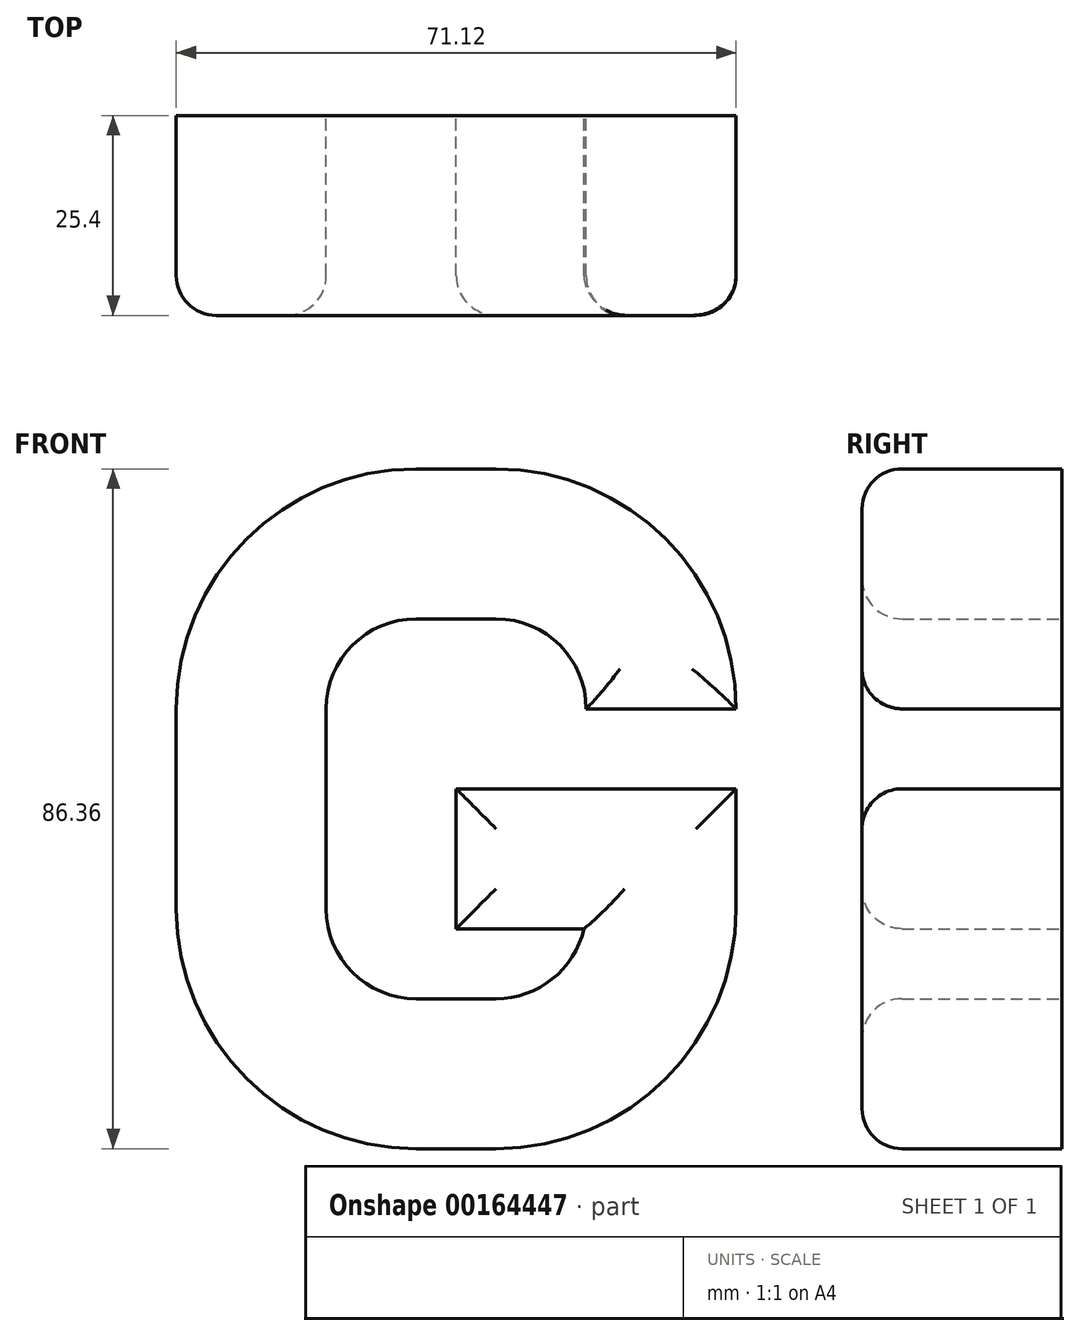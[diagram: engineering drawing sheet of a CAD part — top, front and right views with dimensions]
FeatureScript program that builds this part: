
annotation { "Feature Type Name" : "Feature", "Feature Type Description" : "" }
export const myFeature = defineFeature(function(context is Context, id is Id, definition is map)
    precondition{}
    {
        {
            var Q0;
            Q0=qCreatedBy(makeId("Front.planeOp"),FACE);
            var sketch = newSketch(context, id + "F0", { "sketchPlane" : qUnion([Q0])});
            skLineSegment(sketch, "E0.bottom", {"start": v(-5.08, 43.18) * mm, "end": v(5.08, 43.18) * mm});
            skLineSegment(sketch, "E0.top", {"start": v(-5.08, -43.18) * mm, "end": v(5.08, -43.18) * mm});
            skLineSegment(sketch, "E0.left", {"start": v(-35.56, 12.7) * mm, "end": v(-35.56, -12.7) * mm});
            skLineSegment(sketch, "E0.right", {"start": v(35.56, 0) * mm, "end": v(35.56, -12.7) * mm});
            skPoint(sketch, "E1.visualSharp", {"position": v(-35.56, 43.18) * mm});
            skArc(sketch, "E1.filletArc", {"start": v(-5.08, 43.18) * mm, "mid": v(-26.63, 34.25) * mm, "end": v(-35.56, 12.7) * mm});
            skPoint(sketch, "E2.visualSharp", {"position": v(-35.56, -43.18) * mm});
            skArc(sketch, "E2.filletArc", {"start": v(-35.56, -12.7) * mm, "mid": v(-26.63, -34.25) * mm, "end": v(-5.08, -43.18) * mm});
            skPoint(sketch, "E3.visualSharp", {"position": v(35.56, 43.18) * mm});
            skArc(sketch, "E3.filletArc", {"start": v(35.56, 12.7) * mm, "mid": v(26.63, 34.25) * mm, "end": v(5.08, 43.18) * mm});
            skPoint(sketch, "E4.visualSharp", {"position": v(35.56, -43.18) * mm});
            skArc(sketch, "E4.filletArc", {"start": v(5.08, -43.18) * mm, "mid": v(26.63, -34.25) * mm, "end": v(35.56, -12.7) * mm});
            skLineSegment(sketch, "E5.0", {"start": v(-5.08, -24.13) * mm, "end": v(5.08, -24.13) * mm});
            skArc(sketch, "E5.1", {"start": v(-16.51, -12.7) * mm, "mid": v(-13.16, -20.78) * mm, "end": v(-5.08, -24.13) * mm});
            skArc(sketch, "E5.2", {"start": v(5.08, -24.13) * mm, "mid": v(12.2, -21.64) * mm, "end": v(16.22, -15.24) * mm});
            skLineSegment(sketch, "E5.3", {"start": v(-16.51, 12.7) * mm, "end": v(-16.51, -12.7) * mm});
            skArc(sketch, "E5.5", {"start": v(16.51, 12.7) * mm, "mid": v(13.16, 20.78) * mm, "end": v(5.08, 24.13) * mm});
            skLineSegment(sketch, "E5.6", {"start": v(-5.08, 24.13) * mm, "end": v(5.08, 24.13) * mm});
            skArc(sketch, "E5.7", {"start": v(-5.08, 24.13) * mm, "mid": v(-13.16, 20.78) * mm, "end": v(-16.51, 12.7) * mm});
            skLineSegment(sketch, "E6", {"start": v(16.51, 12.7) * mm, "end": v(35.56, 12.7) * mm});
            skLineSegment(sketch, "E7", {"start": v(0, 0) * mm, "end": v(0, -12.7) * mm});
            skLineSegment(sketch, "E8", {"start": v(0, -12.7) * mm, "end": v(0, -15.24) * mm});
            skLineSegment(sketch, "E9", {"start": v(0, -15.24) * mm, "end": v(16.22, -15.24) * mm});
            skLineSegment(sketch, "E10", {"start": v(0, 0) * mm, "end": v(0, 2.54) * mm});
            skLineSegment(sketch, "E11", {"start": v(0, 2.54) * mm, "end": v(35.56, 2.54) * mm});
            skLineSegment(sketch, "E12", {"start": v(35.56, 0) * mm, "end": v(35.56, 2.54) * mm});
            skSolve(sketch);
        }
        {
            var Q0;
            Q0=makeQuery(id+"F0.imprint","IMPRINT",FACE,{"disambiguationData":[TD([[makeQuery(id+"F0.imprint","IMPRINT",EDGE,{"derivedFrom":sQuery(id+"F0.wireOp",EDGE,"E0.bottom")}),-1.0]])]});
            extrude(context, id + "F1", {"entities" : qUnion([Q0]), "depth" : 25.4 * mm});
        }
        {
            var Q0;
            Q0=makeQuery(id+"F1.opExtrude","CAP_EDGE",EDGE,{"disambiguationData":[OSD([sQuery(id+"F0.wireOp",EDGE,"E3.filletArc")])],"isStart":false});
            var Q1;
            Q1=makeQuery(id+"F1.opExtrude","CAP_EDGE",EDGE,{"disambiguationData":[OSD([sQuery(id+"F0.wireOp",EDGE,"E5.1")])],"isStart":false});
            var Q2;
            Q2=makeQuery(id+"F1.opExtrude","CAP_EDGE",EDGE,{"disambiguationData":[OSD([sQuery(id+"F0.wireOp",EDGE,"E9")])],"isStart":false});
            var Q3;
            Q3=makeQuery(id+"F1.opExtrude","CAP_EDGE",EDGE,{"disambiguationData":[OSD([sQuery(id+"F0.wireOp",EDGE,"E7"),sQuery(id+"F0.wireOp",EDGE,"E8"),sQuery(id+"F0.wireOp",EDGE,"E10")])],"isStart":false});
            var Q4;
            Q4=makeQuery(id+"F1.opExtrude","CAP_EDGE",EDGE,{"disambiguationData":[OSD([sQuery(id+"F0.wireOp",EDGE,"E11")])],"isStart":false});
            var Q5;
            Q5=makeQuery(id+"F1.opExtrude","CAP_EDGE",EDGE,{"disambiguationData":[OSD([sQuery(id+"F0.wireOp",EDGE,"E6")])],"isStart":false});
            fillet(context, id + "F2", {"entities" : qUnion([Q0, Q1, Q2, Q3, Q4, Q5]), "radius" : 5.08 * mm, "tangentPropagation" : true, "allowEdgeOverflow" : false});
        }
    });
